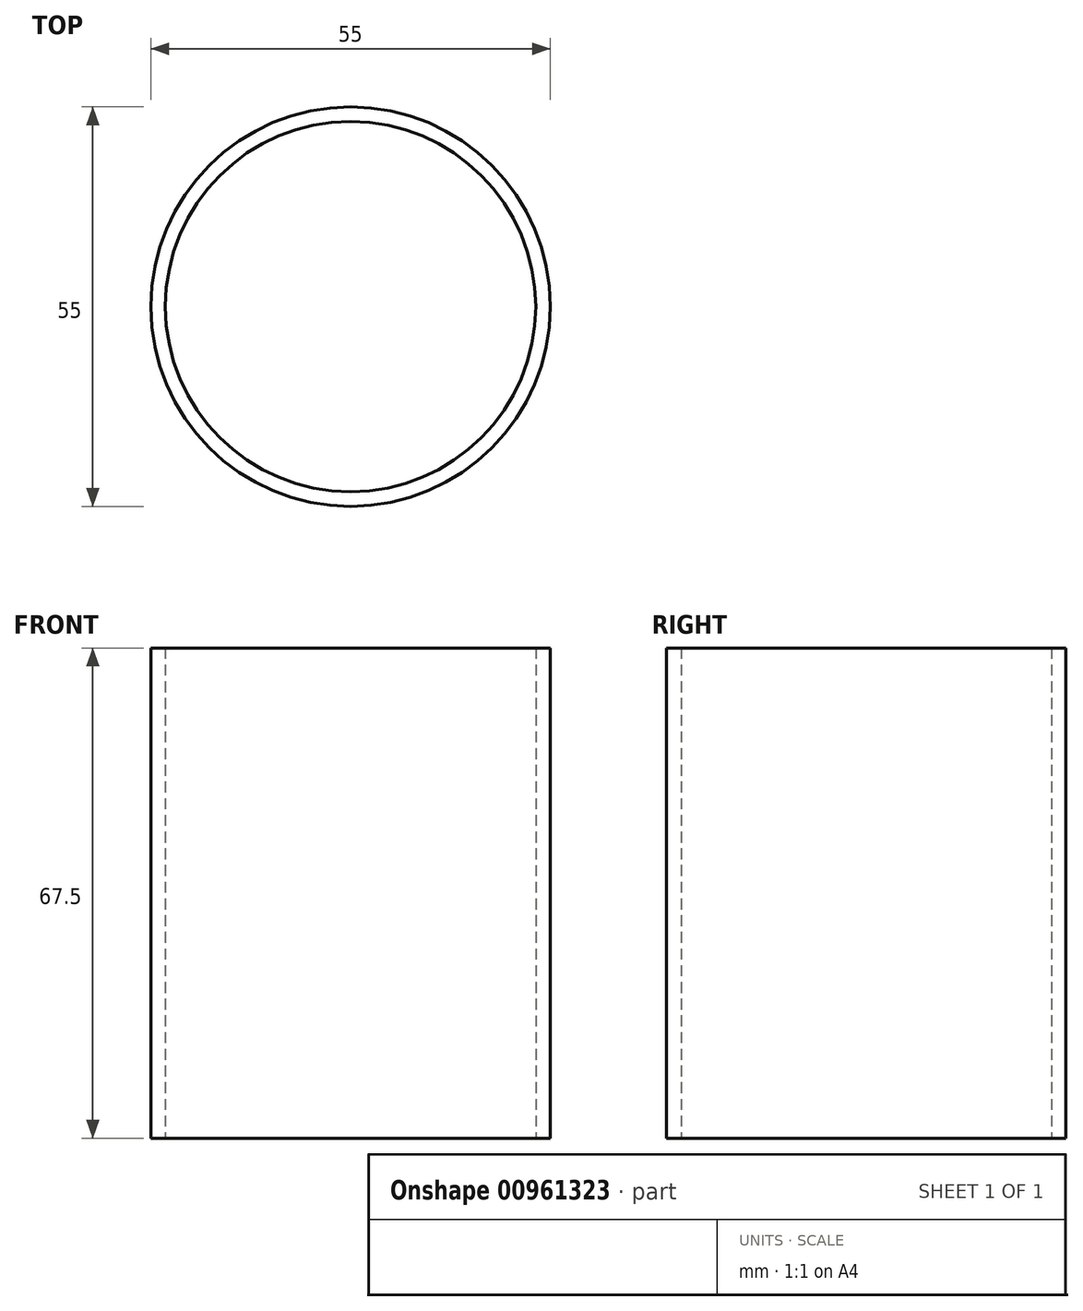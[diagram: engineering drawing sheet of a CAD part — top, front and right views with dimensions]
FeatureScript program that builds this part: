
annotation { "Feature Type Name" : "Feature", "Feature Type Description" : "" }
export const myFeature = defineFeature(function(context is Context, id is Id, definition is map)
    precondition{}
    {
        {
            var Q0;
            Q0=qCreatedBy(makeId("Top.planeOp"),FACE);
            var sketch = newSketch(context, id + "F0", { "sketchPlane" : qUnion([Q0])});
            skCircle(sketch, "E0", {"center": v(0, 0) * mm, "radius": 27.5 * mm});
            skCircle(sketch, "E1", {"center": v(0, 0) * mm, "radius": 25.5 * mm});
            skSolve(sketch);
        }
        {
            var Q0;
            Q0 = qSketchRegion(id + "F0", true);
            extrude(context, id + "F1", {"entities" : qUnion([Q0]), "depth" : 67.5 * mm, "offsetDistance" : 25 * mm});
        }
    });
